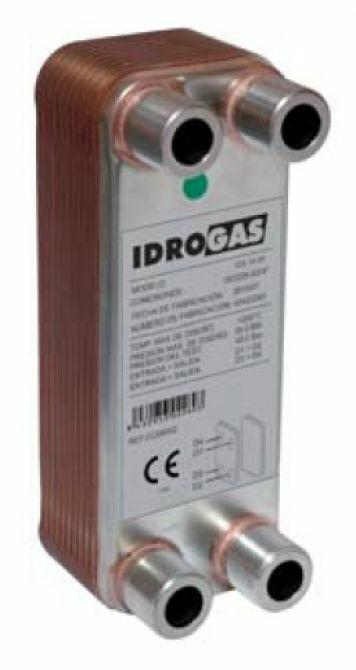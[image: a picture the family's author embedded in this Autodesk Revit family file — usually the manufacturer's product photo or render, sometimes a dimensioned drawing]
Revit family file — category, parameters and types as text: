
# Revit family: IDS14-20_CC08002
name_source: partatom
category: Aparatos eléctricos
revit_build: Autodesk Revit 2016 (Build: 20150220_1215(x64)
units: mm (PartAtom-declared; Revit-internal decimal feet)

## family parameters
Compartido = No
Corte con vacíos al cargar = No
Cota de conector redondo = Diámetro de uso
Mantener orientación de anotación = No
Número OmniClass = 23.80.00.00
Punto de cálculo de habitación = No
Se basa en plano de trabajo = No
Siempre vertical = Sí
Tipo de pieza = Caja de conexiones
Título OmniClass = Electric Power and Lighting

## types (1)
- IDS 14-20
    Caudal máx. = 3,62 m3/h
    Conexiones = 316L acero inox.
    Costo = 0 $
    Código de montaje = CC08002
    Descripción = INTERCAMBIADOR PLACAS TERMOSOLDADO
    Dimensiones = 206 x 78 x ~54 mm
    Fabricante = SALVADOR ESCODA
    Imagen de tipo = IDS-14.jpg
    Material soldadura = 99,99% cobre
    Modelo = IDS 14-20
    Peso = 1,8 Kg
    Placas = 316L acero inox.
    Placas cubierta = 304 acero inox.
    Presión trabajo = 0-30 bar
    Temperatura máx. trabajo = 225 ºC
    URL = www.salvadorescoda.com
